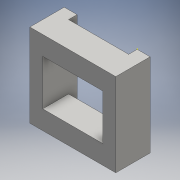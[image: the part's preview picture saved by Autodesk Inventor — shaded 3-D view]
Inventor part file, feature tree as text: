
AUTODESK INVENTOR PART (.ipt)
format: ipt  version: 2016 (Build 200138000, 138)  size: 116,224 bytes
history: native  units: mm
features: sketch x5, extrude x2, other x1
ambient origin geometry x8: Origin, YZ Plane, XZ Plane, XY Plane, X Axis, Y Axis, Z Axis, Center Point
bodies: Body1 (feature_tree)
feature tree (8):
  other  "Bryła1"
  sketch  "Szkic1"
  sketch  "Szkic 3D1"
  sketch  "Szkic 3D2"
  extrude  "Wyciągnięcie proste1"  Depth=97.0mm
  sketch  "Szkic2"
  extrude  "Wyciągnięcie proste2"  Depth=70.0mm
  sketch  "Szkic3"
